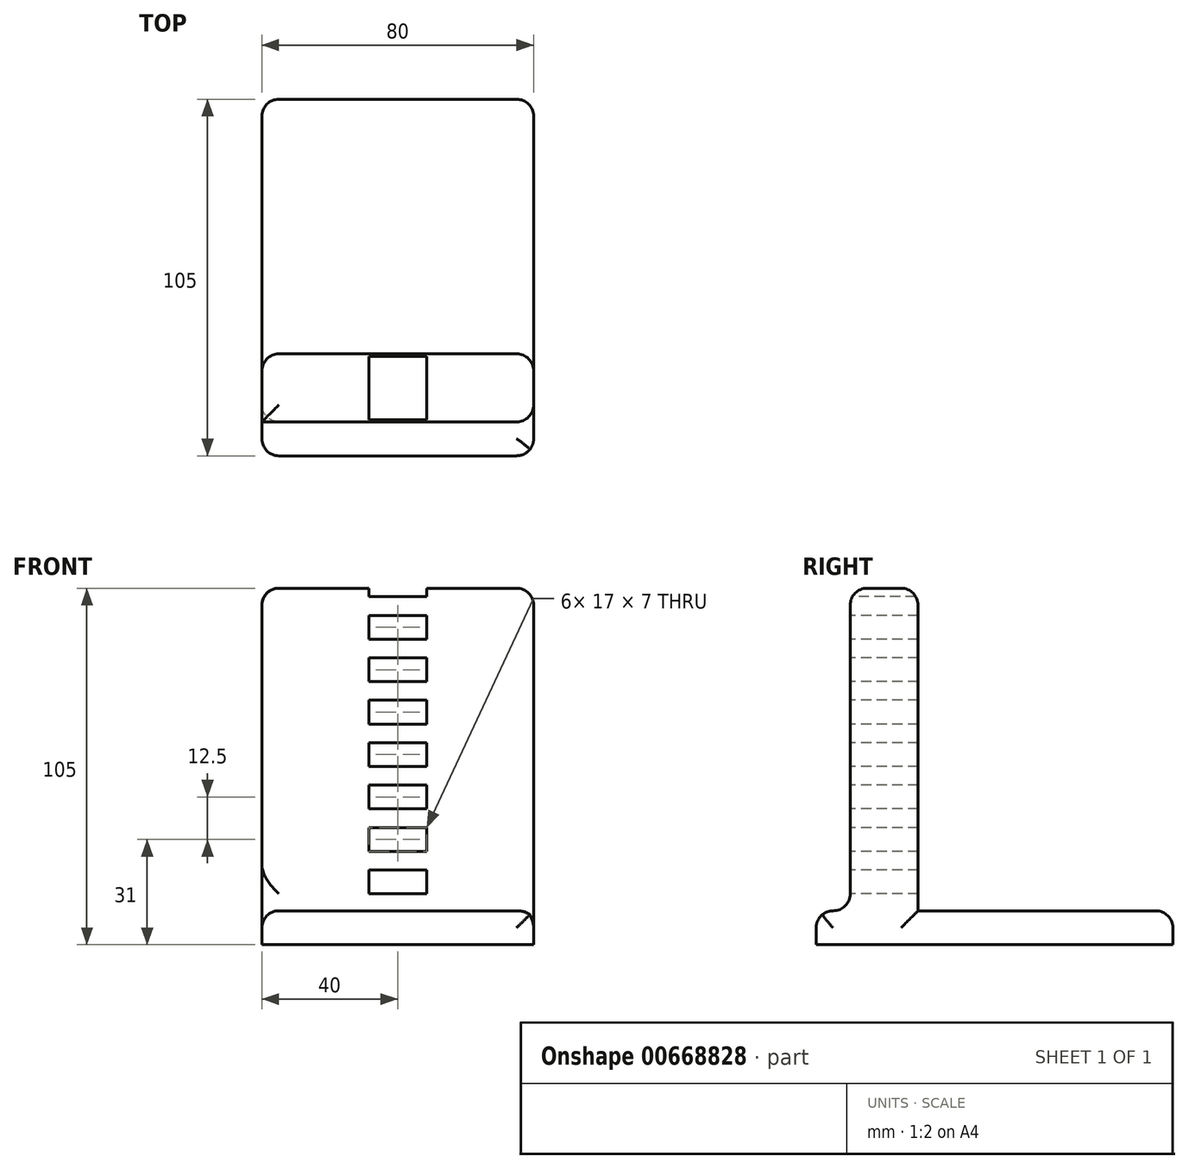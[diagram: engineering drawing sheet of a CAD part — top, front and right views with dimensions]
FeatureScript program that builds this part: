
annotation { "Feature Type Name" : "Feature", "Feature Type Description" : "" }
export const myFeature = defineFeature(function(context is Context, id is Id, definition is map)
    precondition{}
    {
        {
            var Q0;
            Q0=qCreatedBy(makeId("Right.planeOp"),FACE);
            var sketch = newSketch(context, id + "F0", { "sketchPlane" : qUnion([Q0])});
            skLineSegment(sketch, "E0.bottom", {"start": v(-10, 0) * mm, "end": v(10, 0) * mm});
            skLineSegment(sketch, "E0.top", {"start": v(-10, 105) * mm, "end": v(10, 105) * mm});
            skLineSegment(sketch, "E0.left", {"start": v(-10, 0) * mm, "end": v(-10, 105) * mm});
            skLineSegment(sketch, "E0.right", {"start": v(10, 0) * mm, "end": v(10, 105) * mm});
            skLineSegment(sketch, "E1.bottom", {"start": v(-20, 0) * mm, "end": v(85, 0) * mm});
            skLineSegment(sketch, "E1.top", {"start": v(-20, 10) * mm, "end": v(85, 10) * mm});
            skLineSegment(sketch, "E1.left", {"start": v(-20, 0) * mm, "end": v(-20, 10) * mm});
            skLineSegment(sketch, "E1.right", {"start": v(85, 0) * mm, "end": v(85, 10) * mm});
            skSolve(sketch);
        }
        {
            var Q0;
            {var subQ5=sQuery(id+"F0.wireOp",EDGE,"E1.left");Q0=makeQuery(id+"F0.imprint","IMPRINT",FACE,{"disambiguationData":[TD([[makeQuery(id+"F0.imprint","IMPRINT",EDGE,{"derivedFrom":subQ5}),-1.0]])]});}
            var Q1;
            {var subQ5=sQuery(id+"F0.wireOp",EDGE,"E1.right");Q1=makeQuery(id+"F0.imprint","IMPRINT",FACE,{"disambiguationData":[TD([[makeQuery(id+"F0.imprint","IMPRINT",EDGE,{"derivedFrom":subQ5}),1.0]])]});}
            var Q2;
            {var subQ0=sQuery(id+"F0.wireOp",EDGE,"E1.bottom");var subQ1=sQuery(id+"F0.wireOp",EDGE,"E0.left");var subQ2=makeQuery(id+"F0.imprint","INTERSECT",VERTEX,{"derivedFrom":[subQ1,subQ0]});Q2=makeQuery(id+"F0.imprint","IMPRINT",FACE,{"disambiguationData":[TD([[makeQuery(id+"F0.imprint","IMPRINT",EDGE,{"disambiguationData":[TD([[subQ2,-1.0]])],"derivedFrom":subQ1}),-1.0]])]});}
            extrude(context, id + "F1", {"entities" : qUnion([Q0, Q1, Q2]), "endBound" : BoundingType.SYMMETRIC, "depth" : 80 * mm, "offsetDistance" : 25 * mm});
        }
        {
            var Q0;
            {var subQ0=sQuery(id+"F0.wireOp",EDGE,"E0.top");Q0=makeQuery(id+"F0.imprint","IMPRINT",FACE,{"disambiguationData":[TD([[makeQuery(id+"F0.imprint","IMPRINT",EDGE,{"derivedFrom":subQ0}),-1.0]])]});}
            extrude(context, id + "F2", {"entities" : qUnion([Q0]), "operationType" : NewBodyOperationType.ADD, "endBound" : BoundingType.SYMMETRIC, "depth" : 80 * mm, "offsetDistance" : 25 * mm});
        }
        {
            var Q0;
            Q0=makeQuery(id+"F2.opExtrude","SWEPT_FACE",FACE,{"disambiguationData":[OSD([sQuery(id+"F0.wireOp",EDGE,"E0.left")])]});
            var sketch = newSketch(context, id + "F3", { "sketchPlane" : qUnion([Q0])});
            skLineSegment(sketch, "E2", {"start": v(0, 0) * mm, "end": v(0, 105) * mm, "construction": true});
            skLineSegment(sketch, "E3", {"start": v(0, 22) * mm, "end": v(8.5, 22) * mm});
            skLineSegment(sketch, "E4", {"start": v(8.5, 22) * mm, "end": v(8.5, 15) * mm});
            skLineSegment(sketch, "E5", {"start": v(8.5, 15) * mm, "end": v(0, 15) * mm});
            skLineSegment(sketch, "E6.MirrorCS", {"start": v(-8.5, 22) * mm, "end": v(-8.5, 15) * mm});
            skLineSegment(sketch, "E7.MirrorCS", {"start": v(0, 22) * mm, "end": v(-8.5, 22) * mm});
            skLineSegment(sketch, "E8.MirrorCS", {"start": v(-8.5, 15) * mm, "end": v(0, 15) * mm});
            skLineSegment(sketch, "E9.0.1.0", {"start": v(-8.5, 27.5) * mm, "end": v(0, 27.5) * mm});
            skLineSegment(sketch, "E9.0.1.1", {"start": v(0, 34.5) * mm, "end": v(-8.5, 34.5) * mm});
            skLineSegment(sketch, "E9.0.1.2", {"start": v(8.5, 27.5) * mm, "end": v(0, 27.5) * mm});
            skLineSegment(sketch, "E9.0.1.3", {"start": v(0, 34.5) * mm, "end": v(8.5, 34.5) * mm});
            skLineSegment(sketch, "E9.0.1.4", {"start": v(0, 34.5) * mm, "end": v(-8.5, 34.5) * mm});
            skLineSegment(sketch, "E9.0.1.5", {"start": v(-8.5, 34.5) * mm, "end": v(-8.5, 27.5) * mm});
            skLineSegment(sketch, "E9.0.1.6", {"start": v(8.5, 34.5) * mm, "end": v(8.5, 27.5) * mm});
            skLineSegment(sketch, "E9.0.2.0", {"start": v(-8.5, 40) * mm, "end": v(0, 40) * mm});
            skLineSegment(sketch, "E9.0.2.1", {"start": v(0, 47) * mm, "end": v(-8.5, 47) * mm});
            skLineSegment(sketch, "E9.0.2.2", {"start": v(8.5, 40) * mm, "end": v(0, 40) * mm});
            skLineSegment(sketch, "E9.0.2.3", {"start": v(0, 47) * mm, "end": v(8.5, 47) * mm});
            skLineSegment(sketch, "E9.0.2.4", {"start": v(0, 47) * mm, "end": v(-8.5, 47) * mm});
            skLineSegment(sketch, "E9.0.2.5", {"start": v(-8.5, 47) * mm, "end": v(-8.5, 40) * mm});
            skLineSegment(sketch, "E9.0.2.6", {"start": v(8.5, 47) * mm, "end": v(8.5, 40) * mm});
            skLineSegment(sketch, "E9.0.3.0", {"start": v(-8.5, 52.5) * mm, "end": v(0, 52.5) * mm});
            skLineSegment(sketch, "E9.0.3.1", {"start": v(0, 59.5) * mm, "end": v(-8.5, 59.5) * mm});
            skLineSegment(sketch, "E9.0.3.2", {"start": v(8.5, 52.5) * mm, "end": v(0, 52.5) * mm});
            skLineSegment(sketch, "E9.0.3.3", {"start": v(0, 59.5) * mm, "end": v(8.5, 59.5) * mm});
            skLineSegment(sketch, "E9.0.3.4", {"start": v(0, 59.5) * mm, "end": v(-8.5, 59.5) * mm});
            skLineSegment(sketch, "E9.0.3.5", {"start": v(-8.5, 59.5) * mm, "end": v(-8.5, 52.5) * mm});
            skLineSegment(sketch, "E9.0.3.6", {"start": v(8.5, 59.5) * mm, "end": v(8.5, 52.5) * mm});
            skLineSegment(sketch, "E9.0.4.0", {"start": v(-8.5, 65) * mm, "end": v(0, 65) * mm});
            skLineSegment(sketch, "E9.0.4.1", {"start": v(0, 72) * mm, "end": v(-8.5, 72) * mm});
            skLineSegment(sketch, "E9.0.4.2", {"start": v(8.5, 65) * mm, "end": v(0, 65) * mm});
            skLineSegment(sketch, "E9.0.4.3", {"start": v(0, 72) * mm, "end": v(8.5, 72) * mm});
            skLineSegment(sketch, "E9.0.4.4", {"start": v(0, 72) * mm, "end": v(-8.5, 72) * mm});
            skLineSegment(sketch, "E9.0.4.5", {"start": v(-8.5, 72) * mm, "end": v(-8.5, 65) * mm});
            skLineSegment(sketch, "E9.0.4.6", {"start": v(8.5, 72) * mm, "end": v(8.5, 65) * mm});
            skLineSegment(sketch, "E9.direction1", {"start": v(-8.5, 15) * mm, "end": v(20, 15) * mm, "construction": true});
            skLineSegment(sketch, "E9.direction2", {"start": v(-8.5, 15) * mm, "end": v(-8.5, 27.5) * mm, "construction": true});
            skLineSegment(sketch, "E10.0.0.5", {"start": v(-8.5, 77.5) * mm, "end": v(0, 77.5) * mm});
            skLineSegment(sketch, "E10.3.0.5", {"start": v(0, 84.5) * mm, "end": v(-8.5, 84.5) * mm});
            skLineSegment(sketch, "E10.6.0.5", {"start": v(8.5, 77.5) * mm, "end": v(0, 77.5) * mm});
            skLineSegment(sketch, "E10.9.0.5", {"start": v(0, 84.5) * mm, "end": v(8.5, 84.5) * mm});
            skLineSegment(sketch, "E10.12.0.5", {"start": v(0, 84.5) * mm, "end": v(-8.5, 84.5) * mm});
            skLineSegment(sketch, "E10.15.0.5", {"start": v(-8.5, 84.5) * mm, "end": v(-8.5, 77.5) * mm});
            skLineSegment(sketch, "E10.18.0.5", {"start": v(8.5, 84.5) * mm, "end": v(8.5, 77.5) * mm});
            skLineSegment(sketch, "E11.0.0.6", {"start": v(-8.5, 90) * mm, "end": v(0, 90) * mm});
            skLineSegment(sketch, "E11.3.0.6", {"start": v(0, 97) * mm, "end": v(-8.5, 97) * mm});
            skLineSegment(sketch, "E11.6.0.6", {"start": v(8.5, 90) * mm, "end": v(0, 90) * mm});
            skLineSegment(sketch, "E11.9.0.6", {"start": v(0, 97) * mm, "end": v(8.5, 97) * mm});
            skLineSegment(sketch, "E11.12.0.6", {"start": v(0, 97) * mm, "end": v(-8.5, 97) * mm});
            skLineSegment(sketch, "E11.15.0.6", {"start": v(-8.5, 97) * mm, "end": v(-8.5, 90) * mm});
            skLineSegment(sketch, "E11.18.0.6", {"start": v(8.5, 97) * mm, "end": v(8.5, 90) * mm});
            skLineSegment(sketch, "E12.0.0.7", {"start": v(-8.5, 102.5) * mm, "end": v(0, 102.5) * mm});
            skLineSegment(sketch, "E12.3.0.7", {"start": v(0, 109.5) * mm, "end": v(-8.5, 109.5) * mm});
            skLineSegment(sketch, "E12.6.0.7", {"start": v(8.5, 102.5) * mm, "end": v(0, 102.5) * mm});
            skLineSegment(sketch, "E12.9.0.7", {"start": v(0, 109.5) * mm, "end": v(8.5, 109.5) * mm});
            skLineSegment(sketch, "E12.12.0.7", {"start": v(0, 109.5) * mm, "end": v(-8.5, 109.5) * mm});
            skLineSegment(sketch, "E12.15.0.7", {"start": v(-8.5, 109.5) * mm, "end": v(-8.5, 102.5) * mm});
            skLineSegment(sketch, "E12.18.0.7", {"start": v(8.5, 109.5) * mm, "end": v(8.5, 102.5) * mm});
            skSolve(sketch);
        }
        {
            var Q0;
            Q0 = qSketchRegion(id + "F3", true);
            var Q1;
            Q1=makeQuery(id+"F2.opExtrude","SWEPT_FACE",FACE,{"disambiguationData":[OSD([sQuery(id+"F0.wireOp",EDGE,"E0.right")])]});
            extrude(context, id + "F4", {"entities" : qUnion([Q0]), "operationType" : NewBodyOperationType.REMOVE, "endBound" : BoundingType.UP_TO_SURFACE, "oppositeDirection" : true, "depth" : 25 * mm, "endBoundEntityFace" : qUnion([Q1]), "offsetDistance" : 25 * mm});
        }
        {
            var Q0;
            Q0=makeQuery(id+"F2.opExtrude","SWEPT_EDGE",EDGE,{"disambiguationData":[OSD([sQuery(id+"F0.wireOp",EDGE,"E0.left"),sQuery(id+"F0.wireOp",EDGE,"E1.top")])]});
            var Q1;
            Q1=makeQuery(id+"F1.opExtrude","SWEPT_EDGE",EDGE,{"disambiguationData":[OSD([sQuery(id+"F0.wireOp",EDGE,"E1.top"),sQuery(id+"F0.wireOp",EDGE,"E1.left")])]});
            var Q2;
            {var subQ0=sQuery(id+"F0.wireOp",EDGE,"E1.top");var subQ2=sQuery(id+"F0.wireOp",EDGE,"E1.left");Q2=makeQuery(id+"F2.boolean.opBoolean","SPLIT",EDGE,{"disambiguationData":[TD([makeQuery(id+"F1.opExtrude","SWEPT_FACE",FACE,{"disambiguationData":[OSD([subQ2])]})])],"derivedFrom":makeQuery(id+"F1.opExtrude","CAP_EDGE",EDGE,{"disambiguationData":[OSD([subQ0])],"isStart":true})});}
            var Q3;
            {var subQ0=sQuery(id+"F0.wireOp",EDGE,"E1.top");var subQ2=sQuery(id+"F0.wireOp",EDGE,"E1.right");Q3=makeQuery(id+"F2.boolean.opBoolean","SPLIT",EDGE,{"disambiguationData":[TD([makeQuery(id+"F1.opExtrude","SWEPT_FACE",FACE,{"disambiguationData":[OSD([subQ2])]})])],"derivedFrom":makeQuery(id+"F1.opExtrude","CAP_EDGE",EDGE,{"disambiguationData":[OSD([subQ0])],"isStart":true})});}
            var Q4;
            Q4=makeQuery(id+"F2.opExtrude","SWEPT_EDGE",EDGE,{"disambiguationData":[OSD([sQuery(id+"F0.wireOp",EDGE,"E0.top"),sQuery(id+"F0.wireOp",EDGE,"E0.left")])]});
            var Q5;
            Q5=makeQuery(id+"F2.opExtrude","CAP_EDGE",EDGE,{"disambiguationData":[OSD([sQuery(id+"F0.wireOp",EDGE,"E0.left")])],"isStart":false});
            var Q6;
            Q6=makeQuery(id+"F2.opExtrude","CAP_EDGE",EDGE,{"disambiguationData":[OSD([sQuery(id+"F0.wireOp",EDGE,"E0.top")])],"isStart":true});
            var Q7;
            Q7=makeQuery(id+"F2.opExtrude","CAP_EDGE",EDGE,{"disambiguationData":[OSD([sQuery(id+"F0.wireOp",EDGE,"E0.top")])],"isStart":false});
            var Q8;
            Q8=makeQuery(id+"F2.opExtrude","SWEPT_EDGE",EDGE,{"disambiguationData":[OSD([sQuery(id+"F0.wireOp",EDGE,"E0.top"),sQuery(id+"F0.wireOp",EDGE,"E0.right")])]});
            var Q9;
            Q9=makeQuery(id+"F2.opExtrude","CAP_EDGE",EDGE,{"disambiguationData":[OSD([sQuery(id+"F0.wireOp",EDGE,"E0.right")])],"isStart":true});
            var Q10;
            Q10=makeQuery(id+"F2.opExtrude","CAP_EDGE",EDGE,{"disambiguationData":[OSD([sQuery(id+"F0.wireOp",EDGE,"E0.right")])],"isStart":false});
            var Q11;
            {var subQ0=sQuery(id+"F0.wireOp",EDGE,"E1.right");var subQ1=sQuery(id+"F0.wireOp",EDGE,"E1.top");Q11=makeQuery(id+"F2.boolean.opBoolean","SPLIT",EDGE,{"disambiguationData":[TD([makeQuery(id+"F1.opExtrude","SWEPT_FACE",FACE,{"disambiguationData":[OSD([subQ0])]})])],"derivedFrom":makeQuery(id+"F1.opExtrude","CAP_EDGE",EDGE,{"disambiguationData":[OSD([subQ1])],"isStart":false})});}
            var Q12;
            Q12=makeQuery(id+"F1.opExtrude","SWEPT_EDGE",EDGE,{"disambiguationData":[OSD([sQuery(id+"F0.wireOp",EDGE,"E1.top"),sQuery(id+"F0.wireOp",EDGE,"E1.right")])]});
            var Q13;
            Q13=makeQuery(id+"F1.opExtrude","CAP_EDGE",EDGE,{"disambiguationData":[OSD([sQuery(id+"F0.wireOp",EDGE,"E1.right")])],"isStart":true});
            var Q14;
            Q14=makeQuery(id+"F1.opExtrude","CAP_EDGE",EDGE,{"disambiguationData":[OSD([sQuery(id+"F0.wireOp",EDGE,"E1.right")])],"isStart":false});
            var Q15;
            Q15=makeQuery(id+"F1.opExtrude","CAP_EDGE",EDGE,{"disambiguationData":[OSD([sQuery(id+"F0.wireOp",EDGE,"E1.left")])],"isStart":true});
            var Q16;
            Q16=makeQuery(id+"F1.opExtrude","CAP_EDGE",EDGE,{"disambiguationData":[OSD([sQuery(id+"F0.wireOp",EDGE,"E1.left")])],"isStart":false});
            fillet(context, id + "F5", {"entities" : qUnion([Q0, Q1, Q2, Q3, Q4, Q5, Q6, Q7, Q8, Q9, Q10, Q11, Q12, Q13, Q14, Q15, Q16]), "radius" : 5 * mm, "tangentPropagation" : true, "allowEdgeOverflow" : false});
        }
    });
